# Revit family: Differenzdruckregler 4007_FIX_WE
name_source: partatom
category: Rohrzubehör
units: mm (PartAtom-declared; Revit-internal decimal feet)

## family parameters
Arbeitsebenenbasiert = Nein
Beim Laden mit Abzugskörper schneiden = Nein
Bemaßung runder Anschluss = Durchmesser verwenden
Gemeinsam genutzt = Nein
Immer vertikal = Ja
OmniClass-Nummer = 23.65.55.14.24
OmniClass-Titel = Mixing Valves for Liquid Services
Teiletyp = Unterbricht

## types (1)
- Differenzdruckregler 4007_FIX_WE
    Anwendungsgebiet = Der Differenzdruckregler ist ein Proportionalregler in Geradsitzausführung und arbeitet ohne Hilfsenergie. Der Differenzdruck- Sollwert ist fix auf 23 kPa eingestellt.
    Hersteller = HERZ-Armaturen Ges.m.b.H
    Hinweise zum Material = Im Hanf enthaltenes Ammoniak schädigt Messingventilgehäuse, EPDM Dichtungen werden durch Mineralöle bzw. mineralölhaltige Schmierstoffe aufgequollen und führen somit zum Ausfall der EPDM-Dichtungen. Frost- und Korrosionsschutzmittel auf der Basis von Ethylenglykol sind die entsprechenden Angaben den Unterlagen des Herstellers zu entnehmen.
    Max. Betriebsdruck = 1000000.0 Pa
    Max. Differenzdruck am Gehäuse = 250000.0 Pa
    Max. zulässige Betriebstemperatur = 95 °C
    Medium = Die Verwendung von Ethylen- und Propylenglykol ist im Mischungsverhältnis 25 - 50 % zulässig.
Heizwasserqualität entsprechend ÖNORM H 5195 bzw. VDI-Richtlinie 2035. Als Korrosionsschutz kann Helamin HS 190H oder Waterdos OXA30 verwendet werden.
    Membrane und O-Ringe = EPDM
    Min. Betriebstemperatur (Frostschutz, Graugussgehäuse) = -10 °C
    Min. Betriebstemperatur (Frostschutz, Messinggehäuse) = -20 °C
    Min. Betriebstemperatur (reines Wasser) = 2 °C
    SCRNCODE = 05;03;4
    SCRNSEQ = ARM;ARM_TYP="DIFR";2
    Sollwertfeder = nichtrostender Stahl
    URL = www.herz-armaturen.at
    Ventilgehäuse 4007 = entzinkungsbeständiges Messing
    Vorgabe-Ansicht = 0 mm  [stored 0 ft]
    a1 = 9.5 mm  [stored 0.031168 ft]
    a2 = 21.02 mm
    a3 = 9.5 mm  [stored 0.031168 ft]
    h1 = 20.59 mm
    k1 = 21 mm  [stored 0.0688976 ft]
    k10 = 20.56 mm  [stored 0.0674541 ft]
    k11 = 45 mm  [stored 0.147638 ft]
    k12 = 39.28 mm
    k13 = 14 mm  [stored 0.0459318 ft]
    k14 = 101.66 mm
    k16 = 7.28 mm  [stored 0.0238845 ft]
    k18 = 24.47 mm
    k19 = 24.47 mm
    k2 = 49.08 mm  [stored 0.161024 ft]
    k20 = 70.56 mm
    k21 = 28.72 mm
    k22 = 3.22 mm
    k3 = 63 mm  [stored 0.206693 ft]
    k4 = 142.00°
    k5 = 11.83 mm
    k6 = 8.68 mm
    k7 = 9.45 mm
    k8 = 130.00°
    k9 = 17.65 mm
    m1 = 3.5 mm  [stored 0.0114829 ft]
    m3 = 4 mm  [stored 0.0131234 ft]
    t1 = 24.47 mm

note: [stored X ft] marks values corroborated as IEEE doubles in the binary element streams (Revit-internal decimal feet)
